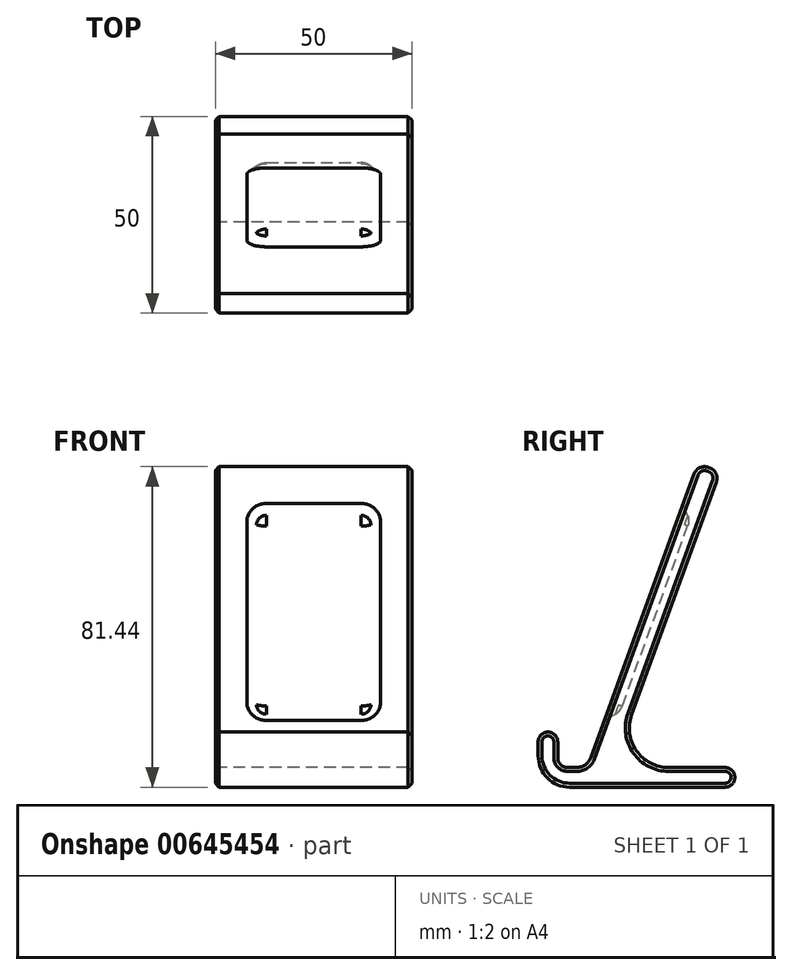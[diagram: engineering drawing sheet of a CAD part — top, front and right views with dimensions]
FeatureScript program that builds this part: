
annotation { "Feature Type Name" : "Feature", "Feature Type Description" : "" }
export const myFeature = defineFeature(function(context is Context, id is Id, definition is map)
    precondition{}
    {
        {
            var Q0;
            Q0=qCreatedBy(makeId("Right.planeOp"),FACE);
            var sketch = newSketch(context, id + "F0", { "sketchPlane" : qUnion([Q0])});
            skLineSegment(sketch, "E0", {"start": v(8, 0) * mm, "end": v(47.5, 0) * mm});
            skLineSegment(sketch, "E1", {"start": v(50, 2.5) * mm, "end": v(50, 2.5) * mm});
            skLineSegment(sketch, "E2", {"start": v(47.5, 5) * mm, "end": v(33.17, 5) * mm});
            skLineSegment(sketch, "E3", {"start": v(23.77, 18.42) * mm, "end": v(45.29, 77.54) * mm});
            skLineSegment(sketch, "E4", {"start": v(43.62, 81.13) * mm, "end": v(43.24, 81.27) * mm});
            skLineSegment(sketch, "E5", {"start": v(39.65, 79.6) * mm, "end": v(13.43, 7.54) * mm});
            skLineSegment(sketch, "E6", {"start": v(9.8, 5) * mm, "end": v(7.5, 5) * mm});
            skLineSegment(sketch, "E7", {"start": v(5, 7.5) * mm, "end": v(5, 11.5) * mm});
            skLineSegment(sketch, "E8", {"start": v(2.5, 14) * mm, "end": v(2.5, 14) * mm});
            skLineSegment(sketch, "E9", {"start": v(0, 11.5) * mm, "end": v(0, 8) * mm});
            skPoint(sketch, "E10.visualSharp", {"position": v(18.89, 5) * mm});
            skArc(sketch, "E10.filletArc", {"start": v(23.77, 18.42) * mm, "mid": v(24.98, 9.26) * mm, "end": v(33.17, 5) * mm});
            skPoint(sketch, "E11.visualSharp", {"position": v(50, 0) * mm});
            skArc(sketch, "E11.filletArc", {"start": v(47.5, 0) * mm, "mid": v(49.27, 0.73) * mm, "end": v(50, 2.5) * mm});
            skPoint(sketch, "E12.visualSharp", {"position": v(50, 5) * mm});
            skArc(sketch, "E12.filletArc", {"start": v(50, 2.5) * mm, "mid": v(49.27, 4.27) * mm, "end": v(47.5, 5) * mm});
            skPoint(sketch, "E13.visualSharp", {"position": v(5, 5) * mm});
            skArc(sketch, "E13.filletArc", {"start": v(5, 7.5) * mm, "mid": v(5.73, 5.73) * mm, "end": v(7.5, 5) * mm});
            skPoint(sketch, "E14.visualSharp", {"position": v(5, 14) * mm});
            skArc(sketch, "E14.filletArc", {"start": v(5, 11.5) * mm, "mid": v(4.27, 13.27) * mm, "end": v(2.5, 14) * mm});
            skPoint(sketch, "E15.visualSharp", {"position": v(0, 14) * mm});
            skArc(sketch, "E15.filletArc", {"start": v(2.5, 14) * mm, "mid": v(0.73, 13.27) * mm, "end": v(0, 11.5) * mm});
            skPoint(sketch, "E16.visualSharp", {"position": v(0, 0) * mm});
            skArc(sketch, "E16.filletArc", {"start": v(0, 8) * mm, "mid": v(2.34, 2.34) * mm, "end": v(8, 0) * mm});
            skPoint(sketch, "E17.visualSharp", {"position": v(12.5, 5) * mm});
            skArc(sketch, "E17.filletArc", {"start": v(9.8, 5) * mm, "mid": v(12.01, 5.7) * mm, "end": v(13.43, 7.54) * mm});
            skPoint(sketch, "E18.visualSharp", {"position": v(40.6, 82.23) * mm});
            skArc(sketch, "E18.filletArc", {"start": v(43.24, 81.27) * mm, "mid": v(41.1, 81.18) * mm, "end": v(39.65, 79.6) * mm});
            skPoint(sketch, "E19.visualSharp", {"position": v(46.25, 80.18) * mm});
            skArc(sketch, "E19.filletArc", {"start": v(45.29, 77.54) * mm, "mid": v(45.2, 79.69) * mm, "end": v(43.62, 81.13) * mm});
            skSolve(sketch);
        }
        {
            var Q0;
            Q0=makeQuery(id+"F0.imprint","IMPRINT",FACE,{"disambiguationData":[TD([[makeQuery(id+"F0.imprint","IMPRINT",EDGE,{"derivedFrom":sQuery(id+"F0.wireOp",EDGE,"E0")}),1.0]])]});
            extrude(context, id + "F1", {"entities" : qUnion([Q0]), "depth" : 50 * mm, "offsetDistance" : 25 * mm});
        }
        {
            var Q0;
            Q0=makeQuery(id+"F1.opExtrude","SWEPT_FACE",FACE,{"disambiguationData":[OSD([sQuery(id+"F0.wireOp",EDGE,"E5")])]});
            var sketch = newSketch(context, id + "F2", { "sketchPlane" : qUnion([Q0])});
            skLineSegment(sketch, "E20.bottom", {"start": v(13, 80.36) * mm, "end": v(37, 80.36) * mm});
            skLineSegment(sketch, "E20.top", {"start": v(13, 21.68) * mm, "end": v(37, 21.68) * mm});
            skLineSegment(sketch, "E20.left", {"start": v(8, 75.36) * mm, "end": v(8, 26.68) * mm});
            skLineSegment(sketch, "E20.right", {"start": v(42, 75.36) * mm, "end": v(42, 26.68) * mm});
            skPoint(sketch, "E21.visualSharp", {"position": v(8, 80.36) * mm});
            skArc(sketch, "E21.filletArc", {"start": v(13, 80.36) * mm, "mid": v(9.46, 78.9) * mm, "end": v(8, 75.36) * mm});
            skPoint(sketch, "E22.visualSharp", {"position": v(42, 80.36) * mm});
            skArc(sketch, "E22.filletArc", {"start": v(42, 75.36) * mm, "mid": v(40.54, 78.9) * mm, "end": v(37, 80.36) * mm});
            skPoint(sketch, "E23.visualSharp", {"position": v(42, 21.68) * mm});
            skArc(sketch, "E23.filletArc", {"start": v(37, 21.68) * mm, "mid": v(40.54, 23.14) * mm, "end": v(42, 26.68) * mm});
            skPoint(sketch, "E24.visualSharp", {"position": v(8, 21.68) * mm});
            skArc(sketch, "E24.filletArc", {"start": v(8, 26.68) * mm, "mid": v(9.46, 23.14) * mm, "end": v(13, 21.68) * mm});
            skSolve(sketch);
        }
        {
            var Q0;
            Q0=makeQuery(id+"F2.imprint","IMPRINT",FACE,{"disambiguationData":[TD([[makeQuery(id+"F2.imprint","IMPRINT",EDGE,{"derivedFrom":sQuery(id+"F2.wireOp",EDGE,"E20.bottom")}),-1.0]])]});
            extrude(context, id + "F3", {"entities" : qUnion([Q0]), "operationType" : NewBodyOperationType.REMOVE, "oppositeDirection" : true, "depth" : 3 * mm, "offsetDistance" : 25 * mm, "hasDraft" : true, "draftAngle" : 50 * degree, "draftPullDirection" : true});
        }
        {
            var Q0;
            Q0=makeQuery(id+"F3.boolean.opBoolean","COPY",EDGE,{"derivedFrom":makeQuery(id+"F3.opExtrude","CAP_EDGE",EDGE,{"disambiguationData":[OSD([sQuery(id+"F2.wireOp",EDGE,"E20.left")])],"isStart":true})});
            var Q1;
            Q1=makeQuery(id+"F3.boolean.opBoolean","COPY",EDGE,{"derivedFrom":makeQuery(id+"F3.opExtrude","CAP_EDGE",EDGE,{"disambiguationData":[OSD([sQuery(id+"F2.wireOp",EDGE,"E20.left")])],"isStart":false})});
            fillet(context, id + "F4", {"entities" : qUnion([Q0, Q1]), "radius" : 4 * mm, "tangentPropagation" : true, "allowEdgeOverflow" : false});
        }
        {
            var Q0;
            Q0=makeQuery(id+"F1.opExtrude","CAP_EDGE",EDGE,{"disambiguationData":[OSD([sQuery(id+"F0.wireOp",EDGE,"E5")])],"isStart":false});
            var Q1;
            Q1=makeQuery(id+"F1.opExtrude","CAP_EDGE",EDGE,{"disambiguationData":[OSD([sQuery(id+"F0.wireOp",EDGE,"E5")])],"isStart":true});
            chamfer(context, id + "F5", {"entities" : qUnion([Q0, Q1]), "width" : 1 * mm, "tangentPropagation" : true});
        }
    });
